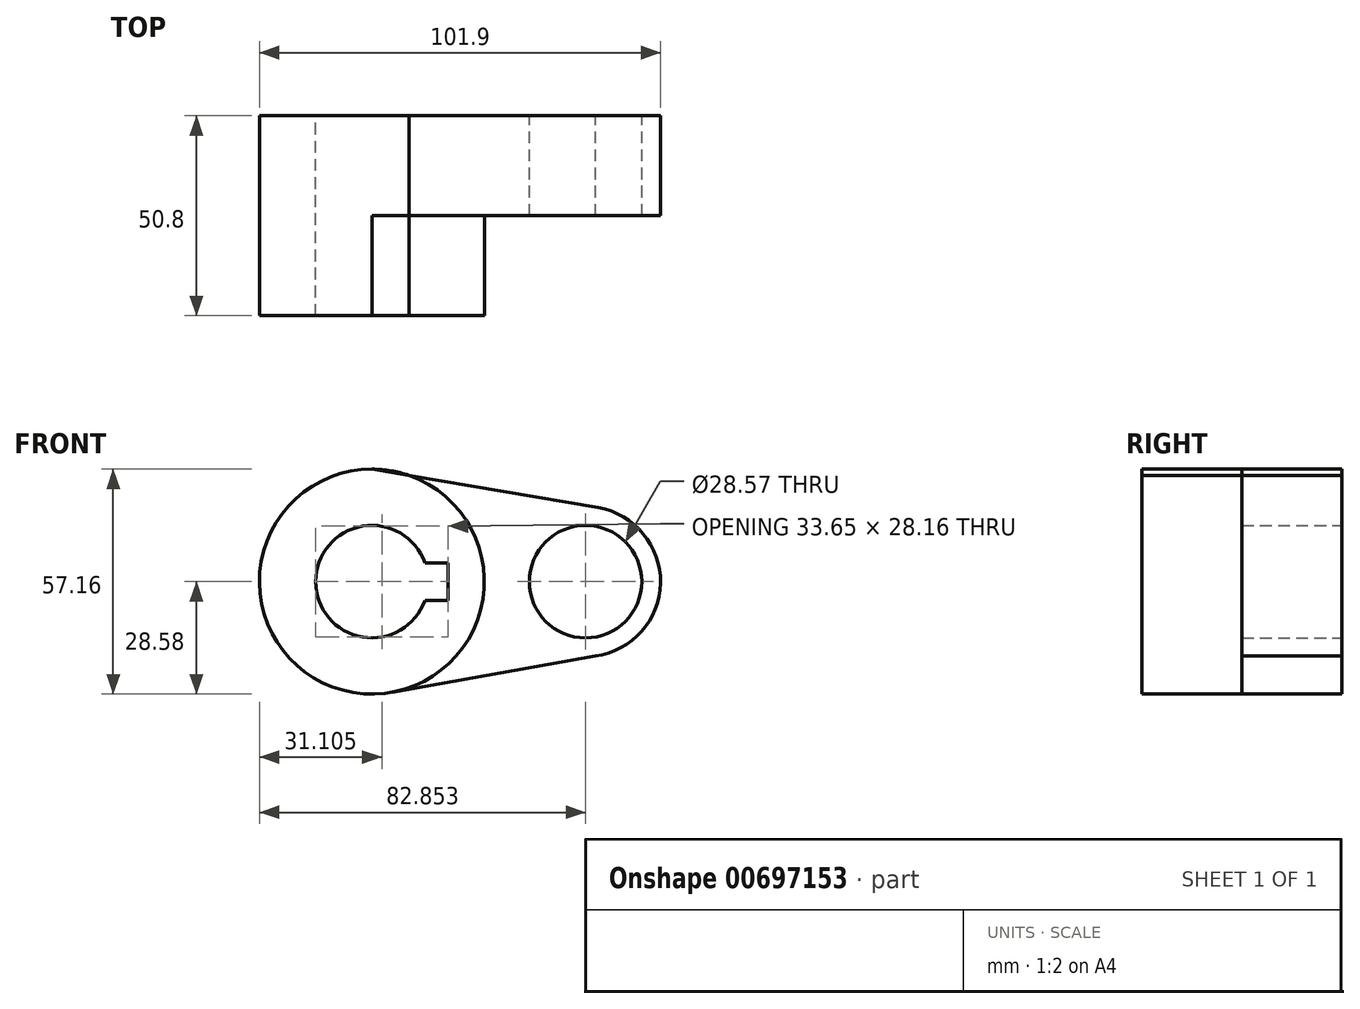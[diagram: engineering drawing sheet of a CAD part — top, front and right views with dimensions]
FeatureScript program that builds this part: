
annotation { "Feature Type Name" : "Feature", "Feature Type Description" : "" }
export const myFeature = defineFeature(function(context is Context, id is Id, definition is map)
    precondition{}
    {
        {
            var Q0;
            Q0=qCreatedBy(makeId("Front.planeOp"),FACE);
            var sketch = newSketch(context, id + "F0", { "sketchPlane" : qUnion([Q0])});
            skCircle(sketch, "E0", {"center": v(0, 0) * mm, "radius": 28.58 * mm});
            skCircle(sketch, "E1", {"center": v(54.28, 0) * mm, "radius": 19.05 * mm});
            skLineSegment(sketch, "E2", {"start": v(0, 28.58) * mm, "end": v(57.48, 18.78) * mm});
            skLineSegment(sketch, "E3", {"start": v(56.81, -18.88) * mm, "end": v(0, -29.03) * mm});
            skCircle(sketch, "E4", {"center": v(0, 0) * mm, "radius": 14.29 * mm});
            skCircle(sketch, "E5", {"center": v(54.28, 0) * mm, "radius": 14.29 * mm});
            skLineSegment(sketch, "E6.left", {"start": v(0.3, 0) * mm, "end": v(0.3, 0) * mm});
            skLineSegment(sketch, "E6.right", {"start": v(-0.3, 0) * mm, "end": v(-0.3, 0) * mm});
            skLineSegment(sketch, "E7.bottom", {"start": v(19.36, -4.76) * mm, "end": v(-18.74, -4.76) * mm});
            skLineSegment(sketch, "E7.top", {"start": v(19.36, 4.76) * mm, "end": v(-18.74, 4.76) * mm});
            skLineSegment(sketch, "E7.left", {"start": v(19.36, -4.76) * mm, "end": v(19.36, 4.76) * mm});
            skLineSegment(sketch, "E7.right", {"start": v(-18.74, -4.76) * mm, "end": v(-18.74, 4.76) * mm});
            skPoint(sketch, "E7.middle", {"position": v(0.3, 0) * mm});
            skSolve(sketch);
        }
        {
            var Q0;
            Q0 = qSketchRegion(id + "F0", true);
            extrude(context, id + "F1", {"entities" : qUnion([Q0]), "depth" : 25.4 * mm, "offsetDistance" : 25.4 * mm});
        }
        {
            var Q0;
            {var subQ5=sQuery(id+"F0.wireOp",EDGE,"E7.right");Q0=makeQuery(id+"F0.imprint","IMPRINT",FACE,{"disambiguationData":[TD([[makeQuery(id+"F0.imprint","IMPRINT",EDGE,{"derivedFrom":subQ5}),-1.0]])]});}
            var Q1;
            {var subQ11=sQuery(id+"F0.wireOp",EDGE,"E7.left");Q1=makeQuery(id+"F0.imprint","IMPRINT",FACE,{"disambiguationData":[TD([[makeQuery(id+"F0.imprint","IMPRINT",EDGE,{"derivedFrom":subQ11}),-1.0]])]});}
            extrude(context, id + "F2", {"entities" : qUnion([Q0, Q1]), "operationType" : NewBodyOperationType.ADD, "depth" : 50.8 * mm, "offsetDistance" : 25.4 * mm});
        }
    });
